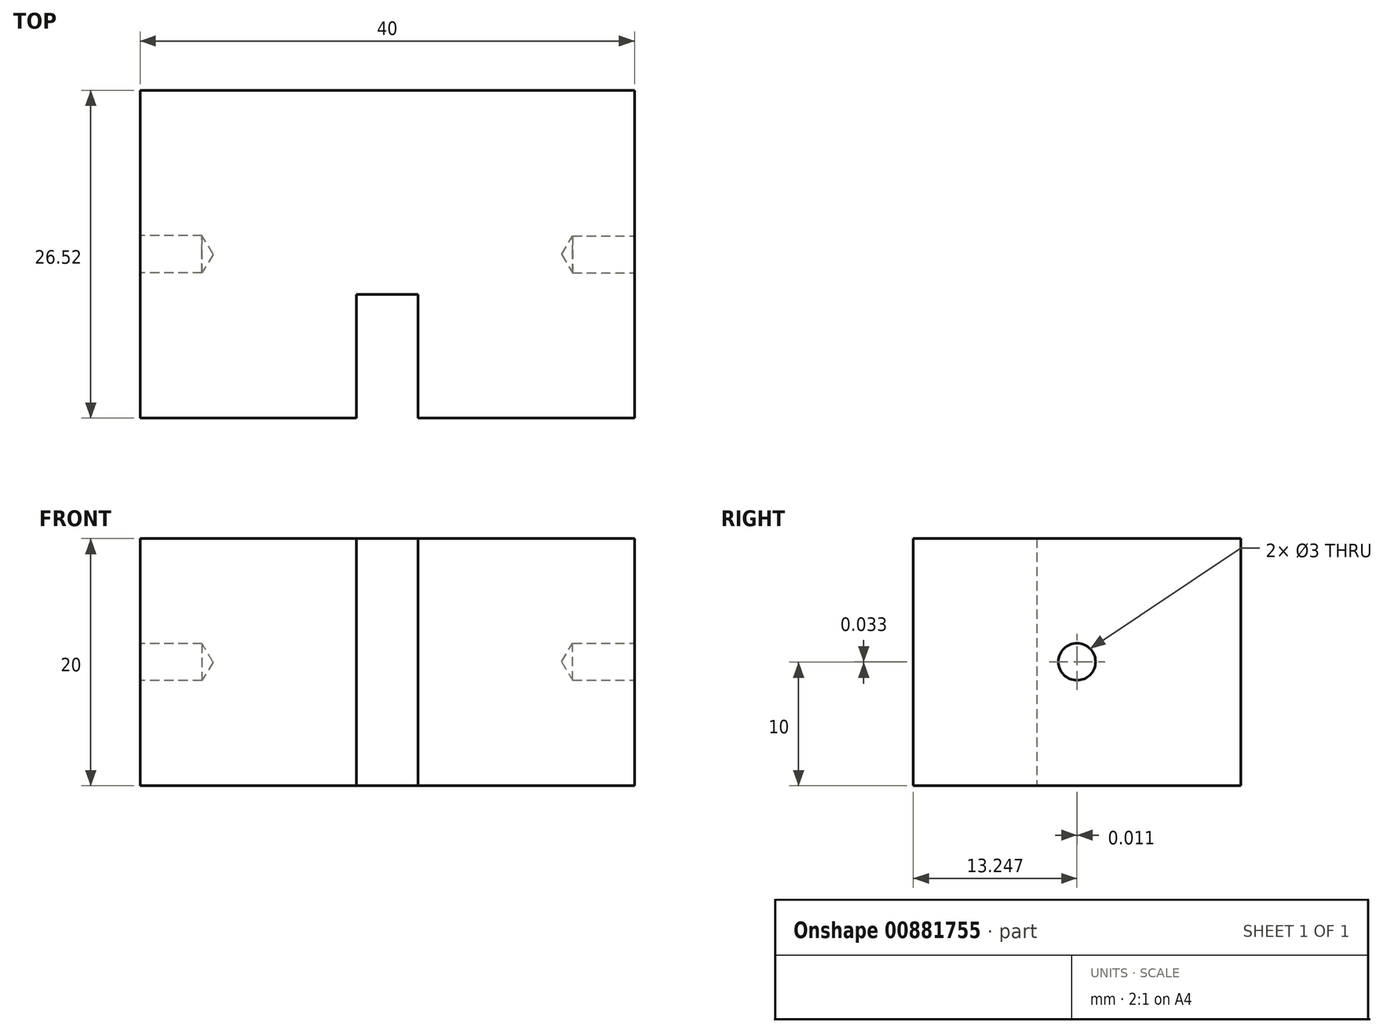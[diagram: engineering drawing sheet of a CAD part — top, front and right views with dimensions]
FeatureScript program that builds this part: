
annotation { "Feature Type Name" : "Feature", "Feature Type Description" : "" }
export const myFeature = defineFeature(function(context is Context, id is Id, definition is map)
    precondition{}
    {
        {
            var Q0;
            Q0=qCreatedBy(makeId("Top.planeOp"),FACE);
            var sketch = newSketch(context, id + "F0", { "sketchPlane" : qUnion([Q0])});
            skLineSegment(sketch, "E0.bottom", {"start": v(-22.5, 18.63) * mm, "end": v(17.5, 18.63) * mm});
            skLineSegment(sketch, "E0.top", {"start": v(-22.5, -7.9) * mm, "end": v(17.5, -7.9) * mm});
            skLineSegment(sketch, "E0.left", {"start": v(-22.5, 18.63) * mm, "end": v(-22.5, -7.9) * mm});
            skLineSegment(sketch, "E0.right", {"start": v(17.5, 18.63) * mm, "end": v(17.5, -7.9) * mm});
            skPoint(sketch, "E1", {"position": v(0, -7.9) * mm});
            skPoint(sketch, "E2", {"position": v(-5, -7.9) * mm});
            skLineSegment(sketch, "E3", {"start": v(-5, -7.9) * mm, "end": v(-5, 2.1) * mm});
            skPoint(sketch, "E3.endSnap0", {"position": v(-2.5, 18.63) * mm});
            skPoint(sketch, "E4", {"position": v(-5, 2.1) * mm});
            skLineSegment(sketch, "E5", {"start": v(-5, 2.1) * mm, "end": v(0, 2.1) * mm});
            skLineSegment(sketch, "E6", {"start": v(0, -7.9) * mm, "end": v(0, 2.1) * mm});
            skPoint(sketch, "E7", {"position": v(0, 2.1) * mm});
            skPoint(sketch, "E8.orphan", {"position": v(-5, 18.63) * mm});
            skLineSegment(sketch, "E9", {"start": v(-5, 2.1) * mm, "end": v(-5, -7.9) * mm});
            skLineSegment(sketch, "E10", {"start": v(0, 2.1) * mm, "end": v(0, -7.9) * mm});
            skLineSegment(sketch, "E11", {"start": v(-5, -7.9) * mm, "end": v(0, -7.9) * mm});
            skSolve(sketch);
        }
        {
            var Q0;
            Q0 = qSketchRegion(id + "F0", true);
            extrude(context, id + "F1", {"entities" : qUnion([Q0]), "depth" : 20 * mm, "offsetDistance" : 25 * mm});
        }
        {
            var Q0;
            {var subQ0=sQuery(id+"F0.wireOp",EDGE,"E5");Q0=makeQuery(id+"F0.imprint","IMPRINT",FACE,{"disambiguationData":[TD([[makeQuery(id+"F0.imprint","IMPRINT",EDGE,{"derivedFrom":subQ0}),-1.0]])]});}
            extrude(context, id + "F2", {"entities" : qUnion([Q0]), "operationType" : NewBodyOperationType.REMOVE, "depth" : 158.6 * mm, "offsetDistance" : 25 * mm});
        }
        {
            var Q0;
            Q0=makeQuery(id+"F1.opExtrude","SWEPT_FACE",FACE,{"disambiguationData":[OSD([sQuery(id+"F0.wireOp",EDGE,"E0.left")])]});
            var sketch = newSketch(context, id + "F3", { "sketchPlane" : qUnion([Q0])});
            skLineSegment(sketch, "E12", {"start": v(7.9, 20) * mm, "end": v(-18.63, 0) * mm});
            skLineSegment(sketch, "E13", {"start": v(-18.63, 0) * mm, "end": v(-18.63, 20) * mm});
            skLineSegment(sketch, "E14", {"start": v(-18.63, 20) * mm, "end": v(7.9, 0) * mm});
            skPoint(sketch, "E15", {"position": v(-5.37, 10) * mm});
            skPoint(sketch, "E16", {"position": v(7.9, 20) * mm});
            skSolve(sketch);
        }
        {
            var Q0;
            Q0=makeQuery(id+"F1.opExtrude","SWEPT_FACE",FACE,{"disambiguationData":[OSD([sQuery(id+"F0.wireOp",EDGE,"E0.right")])]});
            var sketch = newSketch(context, id + "F4", { "sketchPlane" : qUnion([Q0])});
            skPoint(sketch, "E17", {"position": v(5.36, 10.03) * mm});
            skSolve(sketch);
        }
        {
            var Q0;
            Q0=sQuery(id+"F3.wireOp",VERTEX,"E15");
            var Q1;
            Q1=makeQuery(id+"F1.opExtrude","SWEPT_BODY",BODY,{"disambiguationData":[OSD([sQuery(id+"F0.wireOp",EDGE,"E0.bottom"),sQuery(id+"F0.wireOp",EDGE,"E0.top"),sQuery(id+"F0.wireOp",EDGE,"E0.left"),sQuery(id+"F0.wireOp",EDGE,"E0.right"),sQuery(id+"F0.wireOp",EDGE,"E5"),sQuery(id+"F0.wireOp",EDGE,"E5"),sQuery(id+"F0.wireOp",EDGE,"E11"),sQuery(id+"F0.wireOp",EDGE,"E9"),sQuery(id+"F0.wireOp",EDGE,"E10")])]});
            hole(context, id + "F5", {"style" : HoleStyle.SIMPLE, "endStyle" : HoleEndStyle.BLIND, "holeDiameter" : 3 * mm, "majorDiameter" : 5 * mm, "holeDepth" : 5 * mm, "isTappedThrough" : true, "tappedDepth" : 12 * mm, "tapClearance" : 3, "locations" : qUnion([Q0]), "scope" : qUnion([Q1])});
        }
        {
            var Q0;
            Q0=sQuery(id+"F4.wireOp",VERTEX,"E17");
            var Q1;
            Q1=makeQuery(id+"F1.opExtrude","SWEPT_BODY",BODY,{"disambiguationData":[OSD([sQuery(id+"F0.wireOp",EDGE,"E0.bottom"),sQuery(id+"F0.wireOp",EDGE,"E0.top"),sQuery(id+"F0.wireOp",EDGE,"E0.left"),sQuery(id+"F0.wireOp",EDGE,"E0.right"),sQuery(id+"F0.wireOp",EDGE,"E5"),sQuery(id+"F0.wireOp",EDGE,"E5"),sQuery(id+"F0.wireOp",EDGE,"E11"),sQuery(id+"F0.wireOp",EDGE,"E9"),sQuery(id+"F0.wireOp",EDGE,"E10")])]});
            hole(context, id + "F6", {"style" : HoleStyle.SIMPLE, "endStyle" : HoleEndStyle.BLIND, "holeDiameter" : 3 * mm, "majorDiameter" : 5 * mm, "holeDepth" : 5 * mm, "isTappedThrough" : true, "tappedDepth" : 12 * mm, "tapClearance" : 3, "locations" : qUnion([Q0]), "scope" : qUnion([Q1])});
        }
    });
